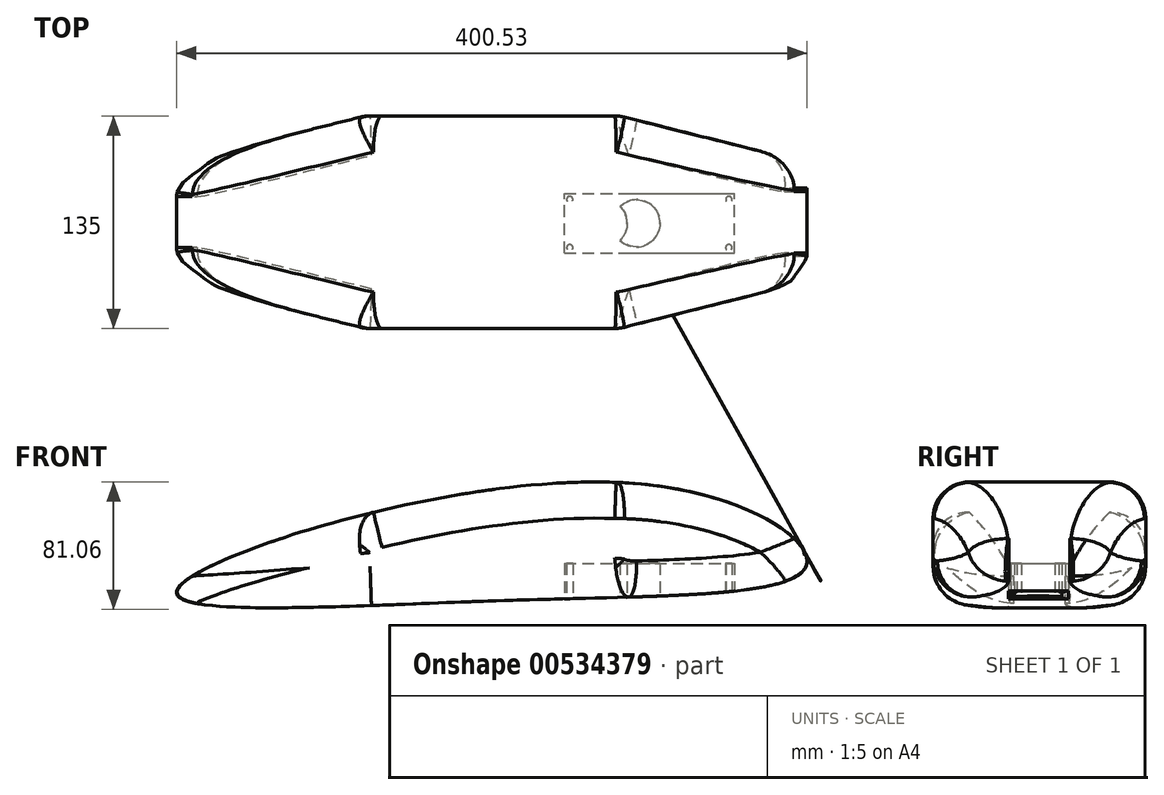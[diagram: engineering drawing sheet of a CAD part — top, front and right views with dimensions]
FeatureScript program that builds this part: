
annotation { "Feature Type Name" : "Feature", "Feature Type Description" : "" }
export const myFeature = defineFeature(function(context is Context, id is Id, definition is map)
    precondition{}
    {
        {
            var Q0;
            Q0=qCreatedBy(makeId("Front.planeOp"),FACE);
            var sketch = newSketch(context, id + "F0", { "sketchPlane" : qUnion([Q0])});
            skFitSpline(sketch, "E0", {"points": [v(138.57, -52.4) * mm, v(24.62, 0) * mm, v(-261.43, -68.66) * mm, v(-48.83, -74.56) * mm, v(138.57, -52.4) * mm]});
            skLineSegment(sketch, "E1", {"start": v(-261.43, -68.66) * mm, "end": v(138.57, -52.4) * mm, "construction": true});
            skSolve(sketch);
        }
        {
            var Q0;
            Q0=makeQuery(id+"F0.imprint","IMPRINT",FACE,{"disambiguationData":[TD([[makeQuery(id+"F0.imprint","IMPRINT",EDGE,{"derivedFrom":sQuery(id+"F0.wireOp",EDGE,"E0")}),1.0]])]});
            extrude(context, id + "F1", {"entities" : qUnion([Q0]), "depth" : 135 * mm, "offsetDistance" : 25 * mm});
        }
        {
            var Q0;
            Q0=qCreatedBy(makeId("Top.planeOp"),FACE);
            var sketch = newSketch(context, id + "F2", { "sketchPlane" : qUnion([Q0])});
            skLineSegment(sketch, "E2", {"start": v(-261.73, 0) * mm, "end": v(-141.73, 0) * mm});
            skLineSegment(sketch, "E3", {"start": v(-261.73, 0) * mm, "end": v(-261.73, -30) * mm});
            skLineSegment(sketch, "E4", {"start": v(-261.73, -30) * mm, "end": v(-141.73, 0) * mm});
            skLineSegment(sketch, "E5", {"start": v(139.62, 0) * mm, "end": v(19.8, 0) * mm});
            skLineSegment(sketch, "E6", {"start": v(19.8, 0) * mm, "end": v(139.62, -30) * mm});
            skLineSegment(sketch, "E7", {"start": v(139.62, -30) * mm, "end": v(139.62, 0) * mm});
            skLineSegment(sketch, "E8", {"start": v(-277.77, -67.5) * mm, "end": v(145.4, -67.5) * mm, "construction": true});
            skLineSegment(sketch, "E9.MirrorCS", {"start": v(-261.73, -105) * mm, "end": v(-141.73, -135) * mm});
            skLineSegment(sketch, "E10.MirrorCS", {"start": v(-261.73, -135) * mm, "end": v(-141.73, -135) * mm});
            skLineSegment(sketch, "E11.MirrorCS", {"start": v(-261.73, -135) * mm, "end": v(-261.73, -105) * mm});
            skLineSegment(sketch, "E12.MirrorCS", {"start": v(19.8, -135) * mm, "end": v(139.62, -105) * mm});
            skLineSegment(sketch, "E13.MirrorCS", {"start": v(139.62, -135) * mm, "end": v(19.8, -135) * mm});
            skLineSegment(sketch, "E14.MirrorCS", {"start": v(139.62, -105) * mm, "end": v(139.62, -135) * mm});
            skSolve(sketch);
        }
        {
            var Q0;
            Q0 = qSketchRegion(id + "F2", true);
            extrude(context, id + "F3", {"entities" : qUnion([Q0]), "operationType" : NewBodyOperationType.REMOVE, "endBound" : BoundingType.SYMMETRIC, "oppositeDirection" : true, "depth" : 200 * mm, "offsetDistance" : 25 * mm});
        }
        {
            var Q0;
            Q0=makeQuery(id+"F3.boolean.opBoolean","SPLIT",EDGE,{"disambiguationData":[OD(1.0)],"derivedFrom":makeQuery(id+"F1.opExtrude","CAP_EDGE",EDGE,{"disambiguationData":[OSD([sQuery(id+"F0.wireOp",EDGE,"E0")])],"isStart":false})});
            var Q1;
            Q1=makeQuery(id+"F3.boolean.opBoolean","INTERSECT",EDGE,{"derivedFrom":[makeQuery(id+"F1.opExtrude","SWEPT_FACE",FACE,{"disambiguationData":[OSD([sQuery(id+"F0.wireOp",EDGE,"E0")])]}),makeQuery(id+"F3.opExtrude","SWEPT_FACE",FACE,{"disambiguationData":[OSD([sQuery(id+"F2.wireOp",EDGE,"E12.MirrorCS")])]})]});
            var Q2;
            Q2=makeQuery(id+"F3.boolean.opBoolean","INTERSECT",EDGE,{"derivedFrom":[makeQuery(id+"F1.opExtrude","SWEPT_FACE",FACE,{"disambiguationData":[OSD([sQuery(id+"F0.wireOp",EDGE,"E0")])]}),makeQuery(id+"F3.opExtrude","SWEPT_FACE",FACE,{"disambiguationData":[OSD([sQuery(id+"F2.wireOp",EDGE,"E6")])]})]});
            var Q3;
            Q3=makeQuery(id+"F3.boolean.opBoolean","SPLIT",EDGE,{"disambiguationData":[OD(1.0)],"derivedFrom":makeQuery(id+"F1.opExtrude","CAP_EDGE",EDGE,{"disambiguationData":[OSD([sQuery(id+"F0.wireOp",EDGE,"E0")])],"isStart":true})});
            fillet(context, id + "F4", {"entities" : qUnion([Q0, Q1, Q2, Q3]), "radius" : 23 * mm, "tangentPropagation" : true, "allowEdgeOverflow" : false});
        }
        {
            var Q0;
            Q0=makeQuery(id+"F3.boolean.opBoolean","SPLIT",EDGE,{"disambiguationData":[OD(0.0)],"derivedFrom":makeQuery(id+"F1.opExtrude","CAP_EDGE",EDGE,{"disambiguationData":[OSD([sQuery(id+"F0.wireOp",EDGE,"E0")])],"isStart":false})});
            var Q1;
            Q1=makeQuery(id+"F3.boolean.opBoolean","SPLIT",EDGE,{"disambiguationData":[OD(0.0)],"derivedFrom":makeQuery(id+"F1.opExtrude","CAP_EDGE",EDGE,{"disambiguationData":[OSD([sQuery(id+"F0.wireOp",EDGE,"E0")])],"isStart":true})});
            fillet(context, id + "F5", {"entities" : qUnion([Q0, Q1]), "radius" : 25 * mm, "tangentPropagation" : true, "allowEdgeOverflow" : false});
        }
        {
            var Q0;
            Q0=makeQuery(id+"F4.opFillet","BLEND_EDGE",EDGE,{"blendedFrom":[makeQuery(id+"F3.boolean.opBoolean","SPLIT",EDGE,{"disambiguationData":[OD(1.0)],"derivedFrom":makeQuery(id+"F1.opExtrude","CAP_EDGE",EDGE,{"disambiguationData":[OSD([sQuery(id+"F0.wireOp",EDGE,"E0")])],"isStart":false})}),makeQuery(id+"F3.boolean.opBoolean","COPY",FACE,{"derivedFrom":makeQuery(id+"F3.opExtrude","SWEPT_FACE",FACE,{"disambiguationData":[OSD([sQuery(id+"F2.wireOp",EDGE,"E9.MirrorCS")])]})})],"blendedInto":[makeQuery(id+"F3.boolean.opBoolean","COPY",FACE,{"derivedFrom":makeQuery(id+"F3.opExtrude","SWEPT_FACE",FACE,{"disambiguationData":[OSD([sQuery(id+"F2.wireOp",EDGE,"E9.MirrorCS")])]})})]});
            var Q1;
            Q1=makeQuery(id+"F3.boolean.opBoolean","INTERSECT",EDGE,{"derivedFrom":[makeQuery(id+"F1.opExtrude","SWEPT_FACE",FACE,{"disambiguationData":[OSD([sQuery(id+"F0.wireOp",EDGE,"E0")])]}),makeQuery(id+"F3.opExtrude","SWEPT_FACE",FACE,{"disambiguationData":[OSD([sQuery(id+"F2.wireOp",EDGE,"E9.MirrorCS")])]})]});
            var Q2;
            Q2=makeQuery(id+"F5.opFillet","BLEND_EDGE",EDGE,{"blendedFrom":[makeQuery(id+"F3.boolean.opBoolean","SPLIT",EDGE,{"disambiguationData":[OD(0.0)],"derivedFrom":makeQuery(id+"F1.opExtrude","CAP_EDGE",EDGE,{"disambiguationData":[OSD([sQuery(id+"F0.wireOp",EDGE,"E0")])],"isStart":false})}),makeQuery(id+"F3.boolean.opBoolean","COPY",FACE,{"derivedFrom":makeQuery(id+"F3.opExtrude","SWEPT_FACE",FACE,{"disambiguationData":[OSD([sQuery(id+"F2.wireOp",EDGE,"E9.MirrorCS")])]})})],"blendedInto":[makeQuery(id+"F3.boolean.opBoolean","COPY",FACE,{"derivedFrom":makeQuery(id+"F3.opExtrude","SWEPT_FACE",FACE,{"disambiguationData":[OSD([sQuery(id+"F2.wireOp",EDGE,"E9.MirrorCS")])]})})]});
            var Q3;
            Q3=makeQuery(id+"F5.opFillet","BLEND_EDGE",EDGE,{"blendedFrom":[makeQuery(id+"F3.boolean.opBoolean","SPLIT",EDGE,{"disambiguationData":[OD(0.0)],"derivedFrom":makeQuery(id+"F1.opExtrude","CAP_EDGE",EDGE,{"disambiguationData":[OSD([sQuery(id+"F0.wireOp",EDGE,"E0")])],"isStart":true})}),makeQuery(id+"F3.boolean.opBoolean","COPY",FACE,{"derivedFrom":makeQuery(id+"F3.opExtrude","SWEPT_FACE",FACE,{"disambiguationData":[OSD([sQuery(id+"F2.wireOp",EDGE,"E4")])]})})],"blendedInto":[makeQuery(id+"F3.boolean.opBoolean","COPY",FACE,{"derivedFrom":makeQuery(id+"F3.opExtrude","SWEPT_FACE",FACE,{"disambiguationData":[OSD([sQuery(id+"F2.wireOp",EDGE,"E4")])]})})]});
            var Q4;
            Q4=makeQuery(id+"F3.boolean.opBoolean","INTERSECT",EDGE,{"derivedFrom":[makeQuery(id+"F1.opExtrude","SWEPT_FACE",FACE,{"disambiguationData":[OSD([sQuery(id+"F0.wireOp",EDGE,"E0")])]}),makeQuery(id+"F3.opExtrude","SWEPT_FACE",FACE,{"disambiguationData":[OSD([sQuery(id+"F2.wireOp",EDGE,"E4")])]})]});
            var Q5;
            Q5=makeQuery(id+"F4.opFillet","BLEND_EDGE",EDGE,{"blendedFrom":[makeQuery(id+"F3.boolean.opBoolean","SPLIT",EDGE,{"disambiguationData":[OD(1.0)],"derivedFrom":makeQuery(id+"F1.opExtrude","CAP_EDGE",EDGE,{"disambiguationData":[OSD([sQuery(id+"F0.wireOp",EDGE,"E0")])],"isStart":true})}),makeQuery(id+"F3.boolean.opBoolean","COPY",FACE,{"derivedFrom":makeQuery(id+"F3.opExtrude","SWEPT_FACE",FACE,{"disambiguationData":[OSD([sQuery(id+"F2.wireOp",EDGE,"E4")])]})})],"blendedInto":[makeQuery(id+"F3.boolean.opBoolean","COPY",FACE,{"derivedFrom":makeQuery(id+"F3.opExtrude","SWEPT_FACE",FACE,{"disambiguationData":[OSD([sQuery(id+"F2.wireOp",EDGE,"E4")])]})})]});
            fillet(context, id + "F6", {"entities" : qUnion([Q0, Q1, Q2, Q3, Q4, Q5]), "radius" : 25 * mm, "tangentPropagation" : true, "allowEdgeOverflow" : false});
        }
        {
            var Q0;
            Q0=qCreatedBy(makeId("Top.planeOp"),FACE);
            cPlane(context, id + "F7", {"entities" : qUnion([Q0]), "cplaneType" : CPlaneType.OFFSET, "offset" : 76 * mm, "oppositeDirection" : true, "width" : 150 * mm, "height" : 150 * mm});
        }
        {
            var Q0;
            Q0=qCreatedBy(id+"F7.planeOp",FACE);
            var sketch = newSketch(context, id + "F8", { "sketchPlane" : qUnion([Q0])});
            skLineSegment(sketch, "E15", {"start": v(-4.05, -68.4) * mm, "end": v(77.57, -68.22) * mm, "construction": true});
            skPoint(sketch, "E16.middle", {"position": v(51.34, -68.28) * mm});
            skPoint(sketch, "E17.middle", {"position": v(30.5, -68.32) * mm});
            skPoint(sketch, "E18.middle", {"position": v(9.67, -68.37) * mm});
            skPoint(sketch, "E19.oppositeSnap0", {"position": v(63.34, -59.3) * mm});
            skPoint(sketch, "E20.endSnap0", {"position": v(63.34, -81.3) * mm});
            skLineSegment(sketch, "E21", {"start": v(30.5, -68.32) * mm, "end": v(30.5, -73.27) * mm, "construction": true});
            skLineSegment(sketch, "E22", {"start": v(51.34, -68.28) * mm, "end": v(51.35, -70.92) * mm, "construction": true});
            skLineSegment(sketch, "E23", {"start": v(50.82, -55.42) * mm, "end": v(51.56, -55.42) * mm});
            skLineSegment(sketch, "E24", {"start": v(50.98, -81.25) * mm, "end": v(51.5, -81.25) * mm});
            skLineSegment(sketch, "E25", {"start": v(30.4, -81.58) * mm, "end": v(30.64, -81.58) * mm});
            skLineSegment(sketch, "E26", {"start": v(30.38, -55.03) * mm, "end": v(30.55, -55.03) * mm});
            skPoint(sketch, "E27.startSnap0", {"position": v(41.03, -77.21) * mm});
            skPoint(sketch, "E27.endSnap0", {"position": v(60.71, -77.98) * mm});
            skPoint(sketch, "E28.startSnap0", {"position": v(20.1, -77.26) * mm});
            skCircle(sketch, "E29", {"center": v(9.67, -68.37) * mm, "radius": 15 * mm});
            skCircle(sketch, "E30", {"center": v(72.11, -68.23) * mm, "radius": 15 * mm});
            skCircle(sketch, "E31", {"center": v(51.34, -68.28) * mm, "radius": 15 * mm});
            skCircle(sketch, "E32", {"center": v(30.56, -68.22) * mm, "radius": 15 * mm});
            skLineSegment(sketch, "E33.bottom", {"start": v(-15.28, -87.22) * mm, "end": v(-15.28, -49.22) * mm});
            skLineSegment(sketch, "E33.top", {"start": v(92.72, -87.22) * mm, "end": v(92.72, -49.22) * mm});
            skLineSegment(sketch, "E33.left", {"start": v(-15.28, -87.22) * mm, "end": v(92.72, -87.22) * mm});
            skLineSegment(sketch, "E33.right", {"start": v(-15.28, -49.22) * mm, "end": v(92.72, -49.22) * mm});
            skCircle(sketch, "E34", {"center": v(-11.78, -83.72) * mm, "radius": 2 * mm});
            skCircle(sketch, "E35.MirrorC", {"center": v(89.22, -83.72) * mm, "radius": 2 * mm});
            skCircle(sketch, "E36.MirrorC", {"center": v(-11.85, -53.1) * mm, "radius": 2 * mm});
            skCircle(sketch, "E37.MirrorC", {"center": v(89.28, -53.1) * mm, "radius": 2 * mm});
            skSolve(sketch);
        }
        {
            var Q0;
            {var subQ0=sQuery(id+"F8.wireOp",EDGE,"E32");var subQ1=sQuery(id+"F8.wireOp",EDGE,"E29");var subQ2=makeQuery(id+"F8.imprint","INTERSECT",VERTEX,{"disambiguationData":[OD(0.0)],"derivedFrom":[subQ1,subQ0]});Q0=makeQuery(id+"F8.imprint","IMPRINT",FACE,{"disambiguationData":[TD([[makeQuery(id+"F8.imprint","IMPRINT",EDGE,{"disambiguationData":[TD([[subQ2,1.0]])],"derivedFrom":subQ1}),1.0]])]});}
            var Q1;
            {var subQ0=sQuery(id+"F8.wireOp",EDGE,"E32");var subQ1=sQuery(id+"F8.wireOp",EDGE,"E29");var subQ2=makeQuery(id+"F8.imprint","INTERSECT",VERTEX,{"disambiguationData":[OD(0.0)],"derivedFrom":[subQ1,subQ0]});Q1=makeQuery(id+"F8.imprint","IMPRINT",FACE,{"disambiguationData":[TD([[makeQuery(id+"F8.imprint","IMPRINT",EDGE,{"disambiguationData":[TD([[subQ2,-1.0]])],"derivedFrom":subQ1}),1.0]])]});}
            var Q2;
            {var subQ0=sQuery(id+"F8.wireOp",EDGE,"E32");var subQ1=sQuery(id+"F8.wireOp",EDGE,"E29");var subQ2=makeQuery(id+"F8.imprint","INTERSECT",VERTEX,{"disambiguationData":[OD(0.0)],"derivedFrom":[subQ1,subQ0]});Q2=makeQuery(id+"F8.imprint","IMPRINT",FACE,{"disambiguationData":[TD([[makeQuery(id+"F8.imprint","IMPRINT",EDGE,{"disambiguationData":[TD([[subQ2,-1.0]])],"derivedFrom":subQ1}),-1.0]])]});}
            var Q3;
            {var subQ0=sQuery(id+"F8.wireOp",EDGE,"E31");var subQ1=sQuery(id+"F8.wireOp",EDGE,"E30");var subQ2=makeQuery(id+"F8.imprint","INTERSECT",VERTEX,{"disambiguationData":[OD(0.0)],"derivedFrom":[subQ1,subQ0]});Q3=makeQuery(id+"F8.imprint","IMPRINT",FACE,{"disambiguationData":[TD([[makeQuery(id+"F8.imprint","IMPRINT",EDGE,{"disambiguationData":[TD([[subQ2,1.0]])],"derivedFrom":subQ1}),-1.0]])]});}
            var Q4;
            {var subQ0=sQuery(id+"F8.wireOp",EDGE,"E32");var subQ1=sQuery(id+"F8.wireOp",EDGE,"E31");var subQ2=makeQuery(id+"F8.imprint","INTERSECT",VERTEX,{"disambiguationData":[OD(0.0)],"derivedFrom":[subQ1,subQ0]});Q4=makeQuery(id+"F8.imprint","IMPRINT",FACE,{"disambiguationData":[TD([[makeQuery(id+"F8.imprint","IMPRINT",EDGE,{"disambiguationData":[TD([[subQ2,1.0]])],"derivedFrom":subQ1}),1.0]])]});}
            var Q5;
            {var subQ0=sQuery(id+"F8.wireOp",EDGE,"E31");var subQ1=sQuery(id+"F8.wireOp",EDGE,"E30");var subQ2=makeQuery(id+"F8.imprint","INTERSECT",VERTEX,{"disambiguationData":[OD(0.0)],"derivedFrom":[subQ1,subQ0]});Q5=makeQuery(id+"F8.imprint","IMPRINT",FACE,{"disambiguationData":[TD([[makeQuery(id+"F8.imprint","IMPRINT",EDGE,{"disambiguationData":[TD([[subQ2,1.0]])],"derivedFrom":subQ1}),1.0]])]});}
            var Q6;
            {var subQ0=sQuery(id+"F8.wireOp",EDGE,"E31");var subQ1=sQuery(id+"F8.wireOp",EDGE,"E30");var subQ2=makeQuery(id+"F8.imprint","INTERSECT",VERTEX,{"disambiguationData":[OD(0.0)],"derivedFrom":[subQ1,subQ0]});Q6=makeQuery(id+"F8.imprint","IMPRINT",FACE,{"disambiguationData":[TD([[makeQuery(id+"F8.imprint","IMPRINT",EDGE,{"disambiguationData":[TD([[subQ2,-1.0]])],"derivedFrom":subQ1}),1.0]])]});}
            extrude(context, id + "F9", {"entities" : qUnion([Q0, Q1, Q2, Q3, Q4, Q5, Q6]), "operationType" : NewBodyOperationType.REMOVE, "depth" : 25 * mm, "offsetDistance" : 25 * mm});
        }
        {
            var Q0;
            Q0=qCreatedBy(makeId("Front.planeOp"),FACE);
            cPlane(context, id + "F10", {"entities" : qUnion([Q0]), "cplaneType" : CPlaneType.OFFSET, "offset" : 30 * mm, "width" : 150 * mm, "height" : 150 * mm});
        }
    });
